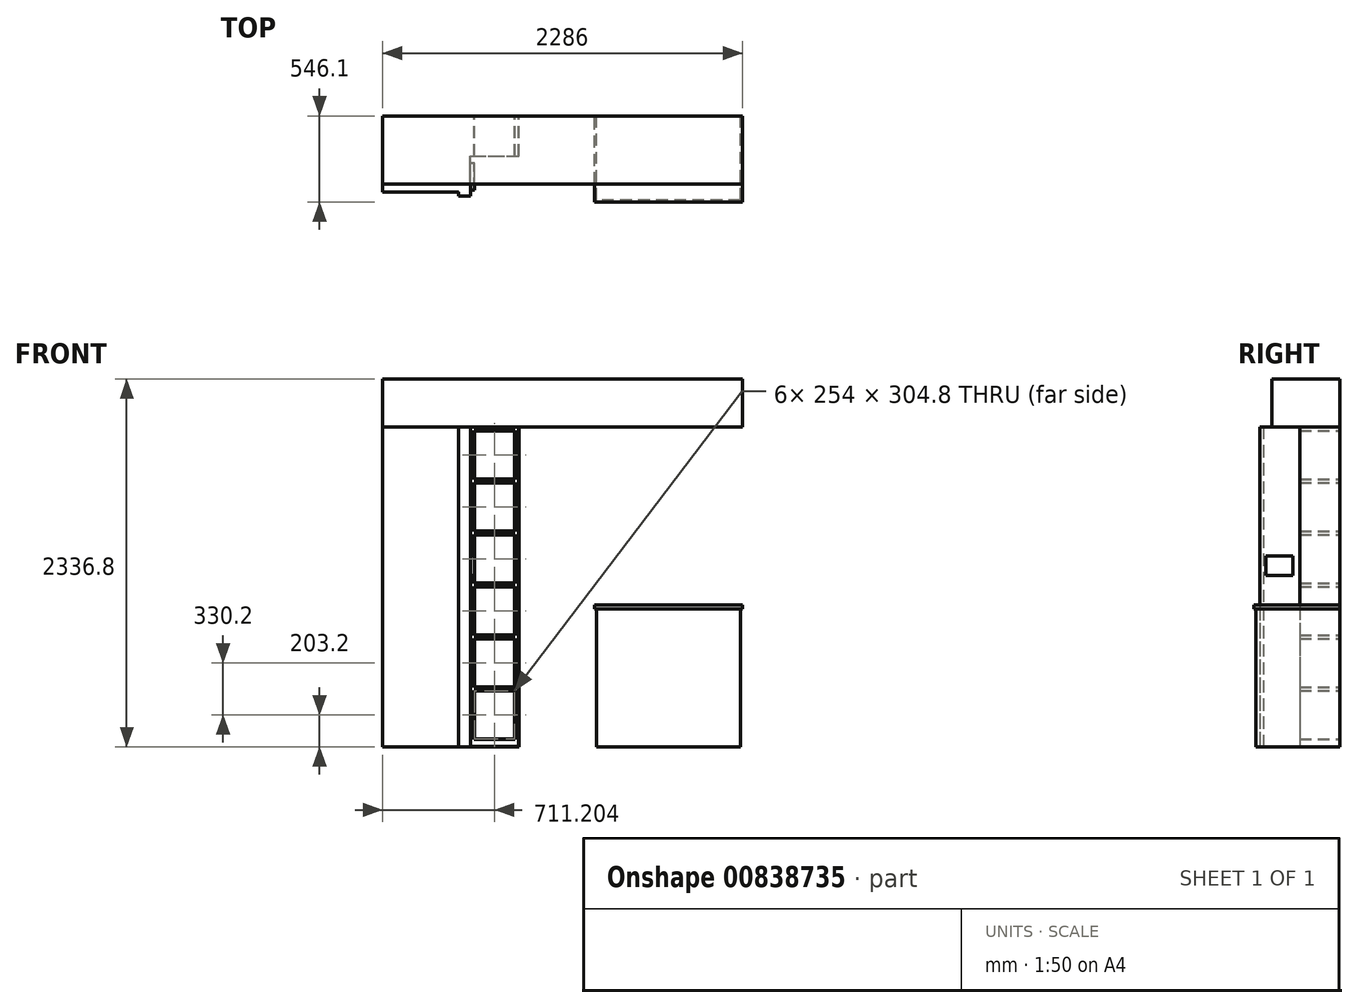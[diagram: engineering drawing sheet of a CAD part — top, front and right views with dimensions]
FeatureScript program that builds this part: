
annotation { "Feature Type Name" : "Feature", "Feature Type Description" : "" }
export const myFeature = defineFeature(function(context is Context, id is Id, definition is map)
    precondition{}
    {
        {
            var Q0;
            Q0=qCreatedBy(makeId("Front.planeOp"),FACE);
            var sketch = newSketch(context, id + "F0", { "sketchPlane" : qUnion([Q0])});
            skLineSegment(sketch, "E0.bottom", {"start": v(-1109.66, -1016) * mm, "end": v(1176.34, -1016) * mm});
            skLineSegment(sketch, "E0.top", {"start": v(-1109.66, 1320.8) * mm, "end": v(1176.34, 1320.8) * mm});
            skLineSegment(sketch, "E0.left", {"start": v(-1109.66, -1016) * mm, "end": v(-1109.66, 1320.8) * mm});
            skLineSegment(sketch, "E0.right", {"start": v(1176.34, -1016) * mm, "end": v(1176.34, 1320.8) * mm});
            skLineSegment(sketch, "E1.top", {"start": v(-627.06, -1016) * mm, "end": v(-550.86, -1016) * mm});
            skLineSegment(sketch, "E1.right", {"start": v(-550.86, 1016) * mm, "end": v(-550.86, -1016) * mm});
            skLineSegment(sketch, "E2.top", {"start": v(-1109.66, 1016) * mm, "end": v(1176.34, 1016) * mm});
            skLineSegment(sketch, "E2.left", {"start": v(-1109.66, 1320.8) * mm, "end": v(-1109.66, 1016) * mm});
            skLineSegment(sketch, "E2.right", {"start": v(1176.34, 1320.8) * mm, "end": v(1176.34, 1016) * mm});
            skLineSegment(sketch, "E3", {"start": v(-627.06, 1016) * mm, "end": v(-627.06, -1016) * mm});
            skLineSegment(sketch, "E4.bottom", {"start": v(1176.34, -139.7) * mm, "end": v(236.54, -139.7) * mm});
            skLineSegment(sketch, "E4.top", {"start": v(1176.34, -114.3) * mm, "end": v(236.54, -114.3) * mm});
            skLineSegment(sketch, "E4.left", {"start": v(1176.34, -139.7) * mm, "end": v(1176.34, -114.3) * mm});
            skLineSegment(sketch, "E4.right", {"start": v(236.54, -139.7) * mm, "end": v(236.54, -114.3) * mm});
            skLineSegment(sketch, "E5.bottom", {"start": v(249.24, -139.7) * mm, "end": v(1163.64, -139.7) * mm});
            skLineSegment(sketch, "E5.top", {"start": v(249.24, -1016) * mm, "end": v(1163.64, -1016) * mm});
            skLineSegment(sketch, "E5.left", {"start": v(249.24, -139.7) * mm, "end": v(249.24, -1016) * mm});
            skLineSegment(sketch, "E5.right", {"start": v(1163.64, -139.7) * mm, "end": v(1163.64, -1016) * mm});
            skLineSegment(sketch, "E6.bottom", {"start": v(-550.86, 1016) * mm, "end": v(-243.52, 1016) * mm});
            skLineSegment(sketch, "E6.top", {"start": v(-550.86, -1016) * mm, "end": v(-243.52, -1016) * mm});
            skLineSegment(sketch, "E6.right", {"start": v(-243.52, 1016) * mm, "end": v(-243.52, -1016) * mm});
            skLineSegment(sketch, "E7.bottom", {"start": v(-525.46, 990.6) * mm, "end": v(-271.46, 990.6) * mm});
            skLineSegment(sketch, "E7.top", {"start": v(-525.46, 685.8) * mm, "end": v(-271.46, 685.8) * mm});
            skLineSegment(sketch, "E7.left", {"start": v(-525.46, 990.6) * mm, "end": v(-525.46, 685.8) * mm});
            skLineSegment(sketch, "E7.right", {"start": v(-271.46, 990.6) * mm, "end": v(-271.46, 685.8) * mm});
            skLineSegment(sketch, "E8.bottom", {"start": v(-525.46, 660.4) * mm, "end": v(-271.46, 660.4) * mm});
            skLineSegment(sketch, "E8.top", {"start": v(-525.46, 355.6) * mm, "end": v(-271.46, 355.6) * mm});
            skLineSegment(sketch, "E8.left", {"start": v(-525.46, 660.4) * mm, "end": v(-525.46, 355.6) * mm});
            skLineSegment(sketch, "E8.right", {"start": v(-271.46, 660.4) * mm, "end": v(-271.46, 355.6) * mm});
            skLineSegment(sketch, "E9.bottom", {"start": v(-525.46, 330.2) * mm, "end": v(-271.46, 330.2) * mm});
            skLineSegment(sketch, "E9.top", {"start": v(-525.46, 25.4) * mm, "end": v(-271.46, 25.4) * mm});
            skLineSegment(sketch, "E9.left", {"start": v(-525.46, 330.2) * mm, "end": v(-525.46, 25.4) * mm});
            skLineSegment(sketch, "E9.right", {"start": v(-271.46, 330.2) * mm, "end": v(-271.46, 25.4) * mm});
            skLineSegment(sketch, "E10.bottom", {"start": v(-525.46, 0) * mm, "end": v(-271.46, 0) * mm});
            skLineSegment(sketch, "E10.top", {"start": v(-525.46, -330.2) * mm, "end": v(-271.46, -330.2) * mm});
            skLineSegment(sketch, "E10.left", {"start": v(-525.46, 0) * mm, "end": v(-525.46, -330.2) * mm});
            skLineSegment(sketch, "E10.right", {"start": v(-271.46, 0) * mm, "end": v(-271.46, -330.2) * mm});
            skLineSegment(sketch, "E11.bottom", {"start": v(-525.46, -304.8) * mm, "end": v(-271.46, -304.8) * mm});
            skLineSegment(sketch, "E11.top", {"start": v(-525.46, -660.4) * mm, "end": v(-271.46, -660.4) * mm});
            skLineSegment(sketch, "E11.left", {"start": v(-525.46, -304.8) * mm, "end": v(-525.46, -660.4) * mm});
            skLineSegment(sketch, "E11.right", {"start": v(-271.46, -304.8) * mm, "end": v(-271.46, -660.4) * mm});
            skPoint(sketch, "E12.oppositeSnap0", {"position": v(-271.46, -482.6) * mm});
            skLineSegment(sketch, "E12.bottom", {"start": v(-525.46, -635) * mm, "end": v(-271.46, -635) * mm});
            skLineSegment(sketch, "E12.top", {"start": v(-525.46, -965.2) * mm, "end": v(-271.46, -965.2) * mm});
            skLineSegment(sketch, "E12.left", {"start": v(-525.46, -635) * mm, "end": v(-525.46, -965.2) * mm});
            skLineSegment(sketch, "E12.right", {"start": v(-271.46, -635) * mm, "end": v(-271.46, -965.2) * mm});
            skSolve(sketch);
        }
        {
            var Q0;
            {var subQ6=sQuery(id+"F0.wireOp",EDGE,"E4.top");Q0=makeQuery(id+"F0.imprint","IMPRINT",FACE,{"disambiguationData":[TD([[makeQuery(id+"F0.imprint","IMPRINT",EDGE,{"derivedFrom":subQ6}),1.0]])]});}
            extrude(context, id + "F1", {"entities" : qUnion([Q0]), "depth" : 546.1 * mm, "offsetDistance" : 25.4 * mm});
        }
        {
            var Q0;
            {var subQ0=sQuery(id+"F0.wireOp",EDGE,"E5.left");Q0=makeQuery(id+"F0.imprint","IMPRINT",FACE,{"disambiguationData":[TD([[makeQuery(id+"F0.imprint","IMPRINT",EDGE,{"derivedFrom":subQ0}),1.0]])]});}
            extrude(context, id + "F2", {"entities" : qUnion([Q0]), "operationType" : NewBodyOperationType.ADD, "depth" : 533.4 * mm, "offsetDistance" : 25.4 * mm});
        }
        {
            var Q0;
            {var subQ3=sQuery(id+"F0.wireOp",EDGE,"E3");Q0=makeQuery(id+"F0.imprint","IMPRINT",FACE,{"disambiguationData":[TD([[makeQuery(id+"F0.imprint","IMPRINT",EDGE,{"derivedFrom":subQ3}),-1.0]])]});}
            extrude(context, id + "F3", {"entities" : qUnion([Q0]), "depth" : 482.6 * mm, "offsetDistance" : 25.4 * mm});
        }
        {
            var Q0;
            {var subQ0=sQuery(id+"F0.wireOp",EDGE,"E1.right");Q0=makeQuery(id+"F0.imprint","IMPRINT",FACE,{"disambiguationData":[TD([[makeQuery(id+"F0.imprint","IMPRINT",EDGE,{"derivedFrom":subQ0}),-1.0]])]});}
            extrude(context, id + "F4", {"entities" : qUnion([Q0]), "operationType" : NewBodyOperationType.ADD, "depth" : 508 * mm, "offsetDistance" : 25.4 * mm});
        }
        {
            var Q0;
            Q0=makeQuery(id+"F4.opExtrude","SWEPT_FACE",FACE,{"disambiguationData":[OSD([sQuery(id+"F0.wireOp",EDGE,"E1.right")])]});
            var sketch = newSketch(context, id + "F5", { "sketchPlane" : qUnion([Q0])});
            skLineSegment(sketch, "E13.bottom", {"start": v(-469.9, 196.47) * mm, "end": v(-298.45, 196.47) * mm});
            skLineSegment(sketch, "E13.top", {"start": v(-469.9, 72.65) * mm, "end": v(-298.45, 72.65) * mm});
            skLineSegment(sketch, "E13.left", {"start": v(-469.9, 196.47) * mm, "end": v(-469.9, 72.65) * mm});
            skLineSegment(sketch, "E13.right", {"start": v(-298.45, 196.47) * mm, "end": v(-298.45, 72.65) * mm});
            skSolve(sketch);
        }
        {
            var Q0;
            Q0=makeQuery(id+"F5.imprint","IMPRINT",FACE,{"disambiguationData":[TD([[makeQuery(id+"F5.imprint","IMPRINT",EDGE,{"derivedFrom":sQuery(id+"F5.wireOp",EDGE,"E13.bottom")}),-1.0]])]});
            extrude(context, id + "F6", {"entities" : qUnion([Q0]), "operationType" : NewBodyOperationType.ADD, "depth" : 25.4 * mm, "offsetDistance" : 25.4 * mm});
        }
        {
            var Q0;
            {var subQ14=sQuery(id+"F0.wireOp",EDGE,"E1.right");Q0=makeQuery(id+"F0.imprint","IMPRINT",FACE,{"disambiguationData":[TD([[makeQuery(id+"F0.imprint","IMPRINT",EDGE,{"derivedFrom":subQ14}),1.0]])]});}
            var Q1;
            {var subQ0=sQuery(id+"F0.wireOp",EDGE,"E10.top");Q1=makeQuery(id+"F0.imprint","IMPRINT",FACE,{"disambiguationData":[TD([[makeQuery(id+"F0.imprint","IMPRINT",EDGE,{"derivedFrom":subQ0}),1.0]])]});}
            var Q2;
            {var subQ0=sQuery(id+"F0.wireOp",EDGE,"E11.top");Q2=makeQuery(id+"F0.imprint","IMPRINT",FACE,{"disambiguationData":[TD([[makeQuery(id+"F0.imprint","IMPRINT",EDGE,{"derivedFrom":subQ0}),1.0]])]});}
            extrude(context, id + "F7", {"entities" : qUnion([Q0, Q1, Q2]), "operationType" : NewBodyOperationType.ADD, "depth" : 254 * mm, "offsetDistance" : 25.4 * mm});
        }
        {
            var Q0;
            {var subQ5=sQuery(id+"F0.wireOp",EDGE,"E0.top");Q0=makeQuery(id+"F0.imprint","IMPRINT",FACE,{"disambiguationData":[TD([[makeQuery(id+"F0.imprint","IMPRINT",EDGE,{"derivedFrom":subQ5}),-1.0]])]});}
            extrude(context, id + "F8", {"entities" : qUnion([Q0]), "operationType" : NewBodyOperationType.ADD, "depth" : 431.8 * mm, "offsetDistance" : 25.4 * mm});
        }
        {
            var Q0;
            Q0=makeQuery(id+"F7.opExtrude","CAP_FACE",FACE,{"disambiguationData":[OSD([sQuery(id+"F0.wireOp",EDGE,"E0.bottom"),sQuery(id+"F0.wireOp",EDGE,"E1.right"),sQuery(id+"F0.wireOp",EDGE,"E2.top"),sQuery(id+"F0.wireOp",EDGE,"E6.right"),sQuery(id+"F0.wireOp",EDGE,"E7.bottom"),sQuery(id+"F0.wireOp",EDGE,"E7.top"),sQuery(id+"F0.wireOp",EDGE,"E7.left"),sQuery(id+"F0.wireOp",EDGE,"E7.right"),sQuery(id+"F0.wireOp",EDGE,"E8.bottom"),sQuery(id+"F0.wireOp",EDGE,"E8.top"),sQuery(id+"F0.wireOp",EDGE,"E8.left"),sQuery(id+"F0.wireOp",EDGE,"E8.right"),sQuery(id+"F0.wireOp",EDGE,"E9.bottom"),sQuery(id+"F0.wireOp",EDGE,"E9.top"),sQuery(id+"F0.wireOp",EDGE,"E9.left"),sQuery(id+"F0.wireOp",EDGE,"E9.right"),sQuery(id+"F0.wireOp",EDGE,"E10.bottom"),sQuery(id+"F0.wireOp",EDGE,"E10.top"),sQuery(id+"F0.wireOp",EDGE,"E10.left"),sQuery(id+"F0.wireOp",EDGE,"E10.right"),sQuery(id+"F0.wireOp",EDGE,"E11.bottom"),sQuery(id+"F0.wireOp",EDGE,"E11.top"),sQuery(id+"F0.wireOp",EDGE,"E11.left"),sQuery(id+"F0.wireOp",EDGE,"E11.right"),sQuery(id+"F0.wireOp",EDGE,"E12.bottom"),sQuery(id+"F0.wireOp",EDGE,"E12.top"),sQuery(id+"F0.wireOp",EDGE,"E12.left"),sQuery(id+"F0.wireOp",EDGE,"E12.right")])],"isStart":false});
            shell(context, id + "F9", {"entities" : qUnion([Q0]), "thickness" : 2.54 * mm});
        }
        {
            var Q0;
            Q0=makeQuery(id+"F1.opExtrude","SWEPT_FACE",FACE,{"disambiguationData":[OSD([sQuery(id+"F0.wireOp",EDGE,"E4.top")])]});
            var sketch = newSketch(context, id + "F10", { "sketchPlane" : qUnion([Q0])});
            skEllipse(sketch, "E14", {"center": v(719.14, -280.3) * mm, "majorRadius": 217.06 * mm, "minorRadius": 137.58 * mm, "majorAxis": v(-1, 0)});
            skSolve(sketch);
        }
        {
            var Q0;
            Q0=sQuery(id+"F10.wireOp",EDGE,"E14");
            extrude(context, id + "F11", {"bodyType" : ToolBodyType.SURFACE, "surfaceEntities" : qUnion([Q0]), "depth" : -127 * mm, "offsetDistance" : 25.4 * mm});
        }
    });
